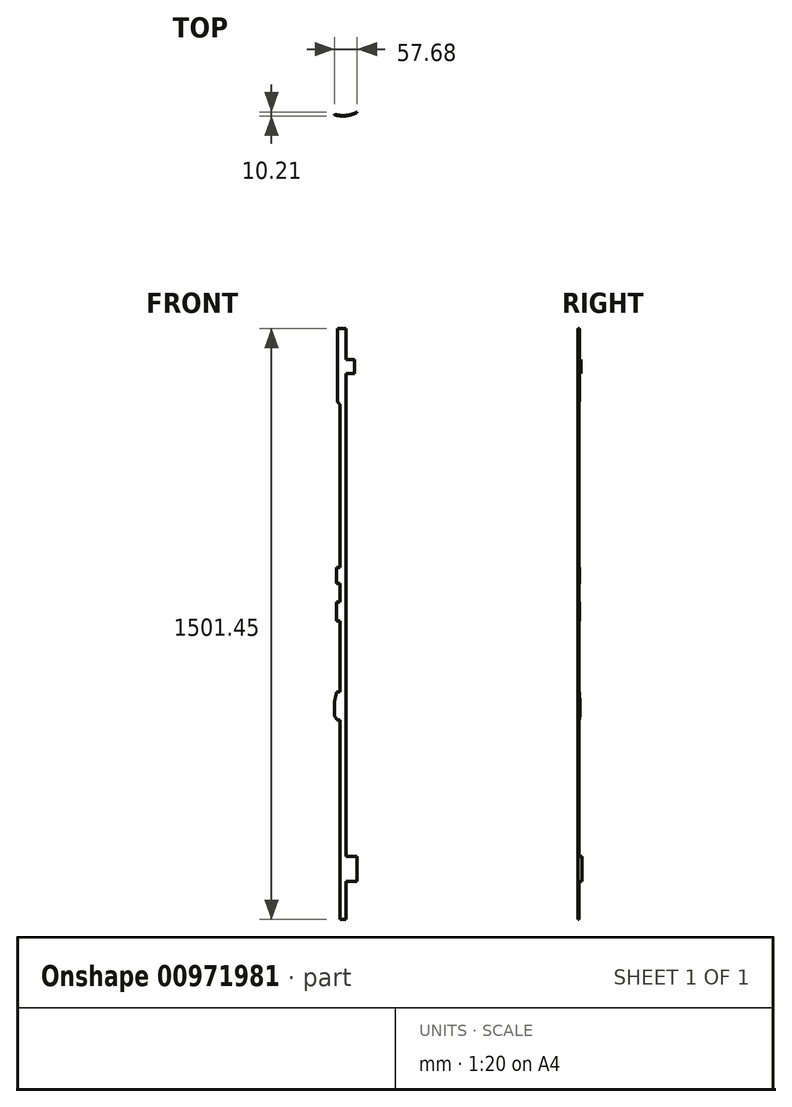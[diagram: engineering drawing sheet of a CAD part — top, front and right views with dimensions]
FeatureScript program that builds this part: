
annotation { "Feature Type Name" : "Feature", "Feature Type Description" : "" }
export const myFeature = defineFeature(function(context is Context, id is Id, definition is map)
    precondition{}
    {
        {
            var Q0;
            Q0=qCreatedBy(makeId("Top.planeOp"),FACE);
            var sketch = newSketch(context, id + "F0", { "sketchPlane" : qUnion([Q0])});
            skLineSegment(sketch, "E0", {"start": v(0, 0) * mm, "end": v(0, 9.42) * mm});
            skLineSegment(sketch, "E1", {"start": v(0, 9.42) * mm, "end": v(38.1, 9.42) * mm});
            skLineSegment(sketch, "E2", {"start": v(38.1, 9.42) * mm, "end": v(35.56, 9.42) * mm});
            skLineSegment(sketch, "E3", {"start": v(0, 9.42) * mm, "end": v(-35.56, 9.42) * mm});
            skArc(sketch, "E4", {"start": v(-38.1, 9.42) * mm, "mid": v(0, -0.79) * mm, "end": v(38.1, 9.42) * mm});
            skLineSegment(sketch, "E5", {"start": v(0, 9.42) * mm, "end": v(0, -0.79) * mm});
            skLineSegment(sketch, "E6", {"start": v(-35.56, 9.42) * mm, "end": v(-38.1, 9.42) * mm});
            skLineSegment(sketch, "E7", {"start": v(33.7, 9.42) * mm, "end": v(0, 9.42) * mm});
            skLineSegment(sketch, "E8", {"start": v(35.56, 9.42) * mm, "end": v(33.7, 9.42) * mm});
            skArc(sketch, "E9", {"start": v(-35.56, 9.42) * mm, "mid": v(0, 0.61) * mm, "end": v(35.56, 9.42) * mm});
            skSolve(sketch);
        }
        {
            var Q0;
            {var subQ1=sQuery(id+"F0.wireOp",EDGE,"E5");Q0=makeQuery(id+"F0.imprint","IMPRINT",FACE,{"disambiguationData":[TD([[makeQuery(id+"F0.imprint","IMPRINT",EDGE,{"derivedFrom":subQ1}),-1.0]])]});}
            var Q1;
            {var subQ0=sQuery(id+"F0.wireOp",EDGE,"E5");Q1=makeQuery(id+"F0.imprint","IMPRINT",FACE,{"disambiguationData":[TD([[makeQuery(id+"F0.imprint","IMPRINT",EDGE,{"derivedFrom":subQ0}),1.0]])]});}
            extrude(context, id + "F1", {"entities" : qUnion([Q0, Q1]), "endBound" : BoundingType.SYMMETRIC, "depth" : 2540 * mm, "offsetDistance" : 25.4 * mm});
        }
        {
            var Q0;
            Q0=qCreatedBy(makeId("Front.planeOp"),FACE);
            var sketch = newSketch(context, id + "F2", { "sketchPlane" : qUnion([Q0])});
            skLineSegment(sketch, "E10.bottom", {"start": v(8.1, -654.38) * mm, "end": v(-8.1, -654.38) * mm});
            skLineSegment(sketch, "E10.top", {"start": v(8.1, 654.38) * mm, "end": v(-8.1, 654.38) * mm});
            skLineSegment(sketch, "E10.left", {"start": v(8.1, -654.38) * mm, "end": v(8.1, 654.38) * mm});
            skLineSegment(sketch, "E10.right", {"start": v(-8.1, -654.38) * mm, "end": v(-8.1, -76.3) * mm});
            skPoint(sketch, "E10.middle", {"position": v(0, 0) * mm});
            skLineSegment(sketch, "E11", {"start": v(-8.1, 654.38) * mm, "end": v(-14.33, 661.14) * mm});
            skLineSegment(sketch, "E12", {"start": v(-14.33, 661.14) * mm, "end": v(-14.33, 847.07) * mm});
            skLineSegment(sketch, "E13", {"start": v(8.1, 654.38) * mm, "end": v(8.1, 847.07) * mm});
            skLineSegment(sketch, "E14", {"start": v(8.1, 847.07) * mm, "end": v(-14.33, 847.07) * mm});
            skLineSegment(sketch, "E15.bottom", {"start": v(29.48, 768.43) * mm, "end": v(-13.26, 768.43) * mm});
            skLineSegment(sketch, "E15.top", {"start": v(29.48, 733.03) * mm, "end": v(-13.26, 733.03) * mm});
            skLineSegment(sketch, "E15.left", {"start": v(29.48, 768.43) * mm, "end": v(29.48, 733.03) * mm});
            skLineSegment(sketch, "E15.right", {"start": v(-13.26, 768.43) * mm, "end": v(-13.26, 733.03) * mm});
            skPoint(sketch, "E15.middle", {"position": v(8.1, 750.73) * mm});
            skLineSegment(sketch, "E16", {"start": v(-9.66, 240.13) * mm, "end": v(-8.1, 240.13) * mm});
            skLineSegment(sketch, "E17.bottom", {"start": v(-8.1, 240.13) * mm, "end": v(-16.17, 240.13) * mm});
            skLineSegment(sketch, "E17.top", {"start": v(-8.1, 199.32) * mm, "end": v(-16.17, 199.32) * mm});
            skLineSegment(sketch, "E17.left", {"start": v(-8.1, 240.13) * mm, "end": v(-8.1, 199.32) * mm});
            skLineSegment(sketch, "E17.right", {"start": v(-16.17, 240.13) * mm, "end": v(-16.17, 199.32) * mm});
            skLineSegment(sketch, "E18", {"start": v(-8.1, 199.32) * mm, "end": v(-8.1, 152) * mm});
            skLineSegment(sketch, "E19.bottom", {"start": v(-8.1, 152) * mm, "end": v(-16.17, 152) * mm});
            skLineSegment(sketch, "E19.top", {"start": v(-8.1, 104.66) * mm, "end": v(-16.17, 104.66) * mm});
            skLineSegment(sketch, "E19.left", {"start": v(-8.1, 152) * mm, "end": v(-8.1, 104.66) * mm});
            skLineSegment(sketch, "E19.right", {"start": v(-16.17, 152) * mm, "end": v(-16.17, 104.66) * mm});
            skLineSegment(sketch, "E20.bottom", {"start": v(8.1, -494.14) * mm, "end": v(36.16, -494.14) * mm});
            skLineSegment(sketch, "E20.top", {"start": v(8.1, -557.08) * mm, "end": v(36.16, -557.08) * mm});
            skLineSegment(sketch, "E20.left", {"start": v(8.1, -494.14) * mm, "end": v(8.1, -557.08) * mm});
            skLineSegment(sketch, "E20.right", {"start": v(36.16, -494.14) * mm, "end": v(36.16, -557.08) * mm});
            skLineSegment(sketch, "E21", {"start": v(8.1, -557.08) * mm, "end": v(-8.1, -557.08) * mm});
            skLineSegment(sketch, "E22", {"start": v(-8.1, -147.6) * mm, "end": v(-8.1, -557.08) * mm});
            skLineSegment(sketch, "E23", {"start": v(-8.1, -76.3) * mm, "end": v(-16.07, -76.3) * mm});
            skLineSegment(sketch, "E24", {"start": v(-16.07, -76.3) * mm, "end": v(-21.52, -100.17) * mm});
            skLineSegment(sketch, "E25", {"start": v(-21.52, -100.17) * mm, "end": v(-21.52, -136.38) * mm});
            skLineSegment(sketch, "E26", {"start": v(-21.52, -136.38) * mm, "end": v(-14.84, -147.6) * mm});
            skLineSegment(sketch, "E27", {"start": v(-14.84, -147.6) * mm, "end": v(-8.1, -147.6) * mm});
            skLineSegment(sketch, "E28", {"start": v(-8.1, -76.3) * mm, "end": v(-8.1, 199.32) * mm});
            skLineSegment(sketch, "E29", {"start": v(-8.1, -76.3) * mm, "end": v(-8.1, -147.6) * mm});
            skLineSegment(sketch, "E30", {"start": v(-8.1, 199.32) * mm, "end": v(-8.1, 654.38) * mm});
            skLineSegment(sketch, "E31", {"start": v(-8.1, 152) * mm, "end": v(-8.1, 152) * mm});
            skLineSegment(sketch, "E32.bottom", {"start": v(-936.44, 1614.42) * mm, "end": v(1043.7, 1614.42) * mm});
            skLineSegment(sketch, "E32.top", {"start": v(-936.44, -1499.19) * mm, "end": v(1043.7, -1499.19) * mm});
            skLineSegment(sketch, "E32.left", {"start": v(-936.44, 1614.42) * mm, "end": v(-936.44, -1499.19) * mm});
            skLineSegment(sketch, "E32.right", {"start": v(1043.7, 1614.42) * mm, "end": v(1043.7, -1499.19) * mm});
            skSolve(sketch);
        }
        {
            var Q0;
            {var subQ18=sQuery(id+"F2.wireOp",EDGE,"E10.bottom");Q0=makeQuery(id+"F2.imprint","IMPRINT",FACE,{"disambiguationData":[TD([[makeQuery(id+"F2.imprint","IMPRINT",EDGE,{"derivedFrom":subQ18}),1.0]])]});}
            extrude(context, id + "F3", {"entities" : qUnion([Q0]), "operationType" : NewBodyOperationType.REMOVE, "endBound" : BoundingType.SYMMETRIC, "oppositeDirection" : true, "depth" : 599.44 * mm, "offsetDistance" : 25.4 * mm});
        }
    });
